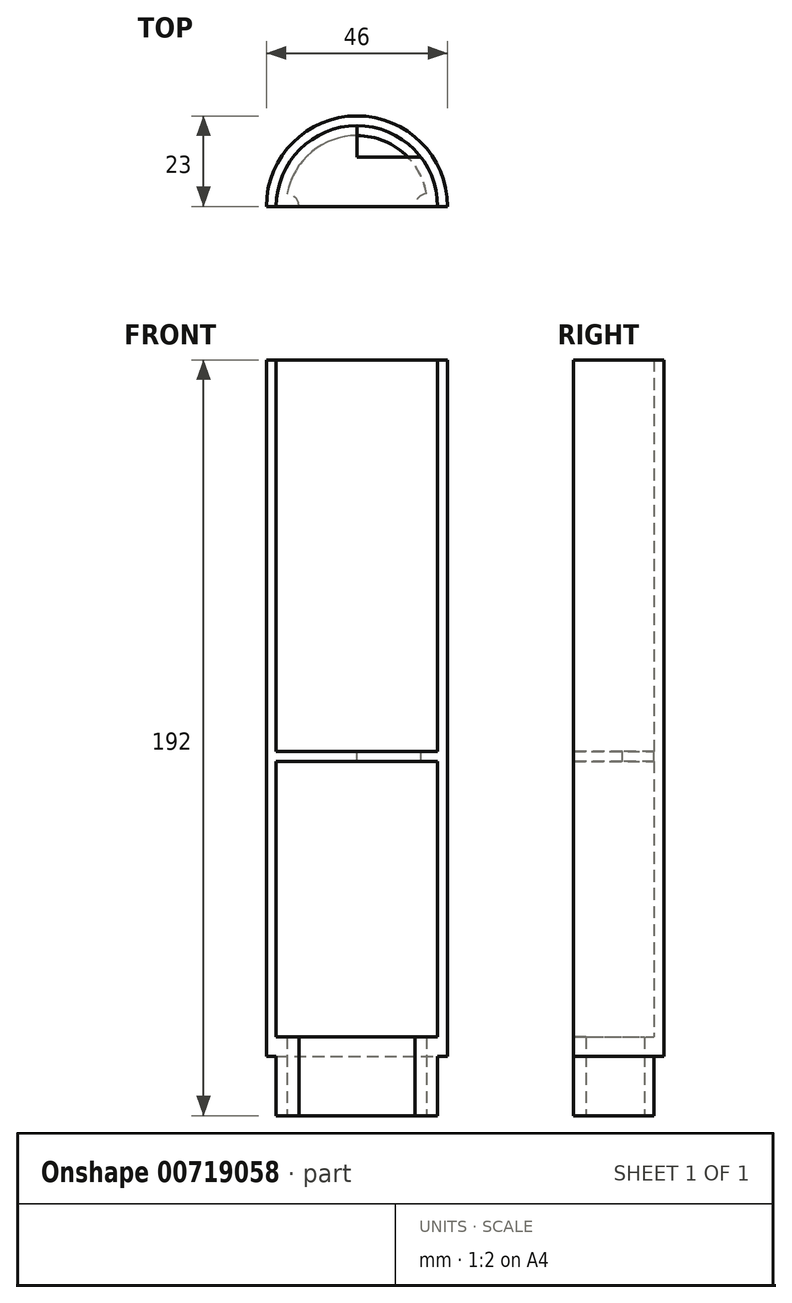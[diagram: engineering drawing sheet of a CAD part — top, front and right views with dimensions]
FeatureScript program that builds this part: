
annotation { "Feature Type Name" : "Feature", "Feature Type Description" : "" }
export const myFeature = defineFeature(function(context is Context, id is Id, definition is map)
    precondition{}
    {
        {
            var Q0;
            Q0=qCreatedBy(makeId("Front.planeOp"),FACE);
            var sketch = newSketch(context, id + "F0", { "sketchPlane" : qUnion([Q0])});
            skLineSegment(sketch, "E0.top", {"start": v(0, 2.5) * mm, "end": v(20.5, 2.5) * mm});
            skLineSegment(sketch, "E0.right", {"start": v(20.5, 102) * mm, "end": v(20.5, 2.5) * mm});
            skLineSegment(sketch, "E1", {"start": v(20.5, 102) * mm, "end": v(23, 102) * mm});
            skLineSegment(sketch, "E2", {"start": v(23, 102) * mm, "end": v(23, 0) * mm});
            skLineSegment(sketch, "E3", {"start": v(0, 0) * mm, "end": v(0, 2.5) * mm});
            skLineSegment(sketch, "E4", {"start": v(23, 0) * mm, "end": v(23, -75) * mm});
            skLineSegment(sketch, "E5", {"start": v(23, -75) * mm, "end": v(20.5, -75) * mm});
            skLineSegment(sketch, "E6", {"start": v(0, 0) * mm, "end": v(20.5, 0) * mm});
            skLineSegment(sketch, "E7", {"start": v(20.5, -75) * mm, "end": v(20.5, -90) * mm});
            skLineSegment(sketch, "E8", {"start": v(20.5, -90) * mm, "end": v(18, -90) * mm});
            skLineSegment(sketch, "E9", {"start": v(18, -90) * mm, "end": v(18, -70) * mm});
            skLineSegment(sketch, "E10", {"start": v(18, -70) * mm, "end": v(20.5, -70) * mm});
            skLineSegment(sketch, "E11", {"start": v(20.5, 0) * mm, "end": v(20.5, -70) * mm});
            skSolve(sketch);
        }
        {
            var Q0;
            Q0 = qSketchRegion(id + "F0", true);
            var Q1;
            Q1=sQuery(id+"F0.wireOp",EDGE,"E3");
            revolve(context, id + "F1", {"surfaceOperationType" : NewSurfaceOperationType.NEW, "entities" : qUnion([Q0]), "axis" : qUnion([Q1]), "revolveType" : RevolveType.FULL});
        }
        {
            var Q0;
            Q0=makeQuery(id+"F1.opRevolve","SWEPT_FACE",FACE,{"disambiguationData":[OSD([sQuery(id+"F0.wireOp",EDGE,"E0.top")])]});
            var sketch = newSketch(context, id + "F2", { "sketchPlane" : qUnion([Q0])});
            skCircle(sketch, "E12", {"center": v(0, 0) * mm, "radius": 20.5 * mm});
            skLineSegment(sketch, "E13", {"start": v(0, 20.5) * mm, "end": v(0, 12.5) * mm});
            skLineSegment(sketch, "E14", {"start": v(0, 12.5) * mm, "end": v(16.25, 12.5) * mm});
            skSolve(sketch);
        }
        {
            var Q0;
            {var subQ0=sQuery(id+"F2.wireOp",EDGE,"E13");Q0=makeQuery(id+"F2.imprint","IMPRINT",FACE,{"disambiguationData":[TD([[makeQuery(id+"F2.imprint","IMPRINT",EDGE,{"derivedFrom":subQ0}),1.0]])]});}
            var Q1;
            Q1=makeQuery(id+"F1.opRevolve","SWEPT_FACE",FACE,{"disambiguationData":[OSD([sQuery(id+"F0.wireOp",EDGE,"E6")])]});
            extrude(context, id + "F3", {"entities" : qUnion([Q0]), "operationType" : NewBodyOperationType.REMOVE, "endBound" : BoundingType.UP_TO_SURFACE, "oppositeDirection" : true, "depth" : 25 * mm, "endBoundEntityFace" : qUnion([Q1]), "offsetDistance" : 25 * mm});
        }
        {
            var Q0;
            Q0=makeQuery(id+"F1.opRevolve","SWEPT_FACE",FACE,{"disambiguationData":[OSD([sQuery(id+"F0.wireOp",EDGE,"E8")])]});
            var sketch = newSketch(context, id + "F4", { "sketchPlane" : qUnion([Q0])});
            skArc(sketch, "E15", {"start": v(-17.7, -3.24) * mm, "mid": v(-14.75, 0) * mm, "end": v(-17.7, 3.24) * mm});
            skArc(sketch, "E16", {"start": v(17.7, 3.24) * mm, "mid": v(14.75, 0) * mm, "end": v(17.7, -3.24) * mm});
            skArc(sketch, "E17", {"start": v(17.7, -3.24) * mm, "mid": v(18, 0) * mm, "end": v(17.7, 3.24) * mm});
            skArc(sketch, "E18", {"start": v(-17.7, -3.24) * mm, "mid": v(-18, 0) * mm, "end": v(-17.7, 3.24) * mm});
            skSolve(sketch);
        }
        {
            var Q0;
            Q0 = qSketchRegion(id + "F4", true);
            var Q1;
            Q1=makeQuery(id+"F1.opRevolve","SWEPT_FACE",FACE,{"disambiguationData":[OSD([sQuery(id+"F0.wireOp",EDGE,"E10")])]});
            extrude(context, id + "F5", {"entities" : qUnion([Q0]), "operationType" : NewBodyOperationType.ADD, "endBound" : BoundingType.UP_TO_SURFACE, "oppositeDirection" : true, "depth" : 25 * mm, "endBoundEntityFace" : qUnion([Q1]), "offsetDistance" : 25 * mm});
        }
        {
            var Q0;
            Q0=makeQuery(id+"F1.opRevolve","SWEPT_FACE",FACE,{"disambiguationData":[OSD([sQuery(id+"F0.wireOp",EDGE,"E1")])]});
            var sketch = newSketch(context, id + "F6", { "sketchPlane" : qUnion([Q0])});
            skLineSegment(sketch, "E19", {"start": v(-23, 0) * mm, "end": v(23, 0) * mm});
            skArc(sketch, "E20", {"start": v(23, 0) * mm, "mid": v(0, -23) * mm, "end": v(-23, 0) * mm});
            skSolve(sketch);
        }
        {
            var Q0;
            Q0 = qSketchRegion(id + "F6", true);
            extrude(context, id + "F7", {"entities" : qUnion([Q0]), "operationType" : NewBodyOperationType.REMOVE, "endBound" : BoundingType.THROUGH_ALL, "oppositeDirection" : true, "depth" : 25 * mm, "offsetDistance" : 25 * mm});
        }
    });
